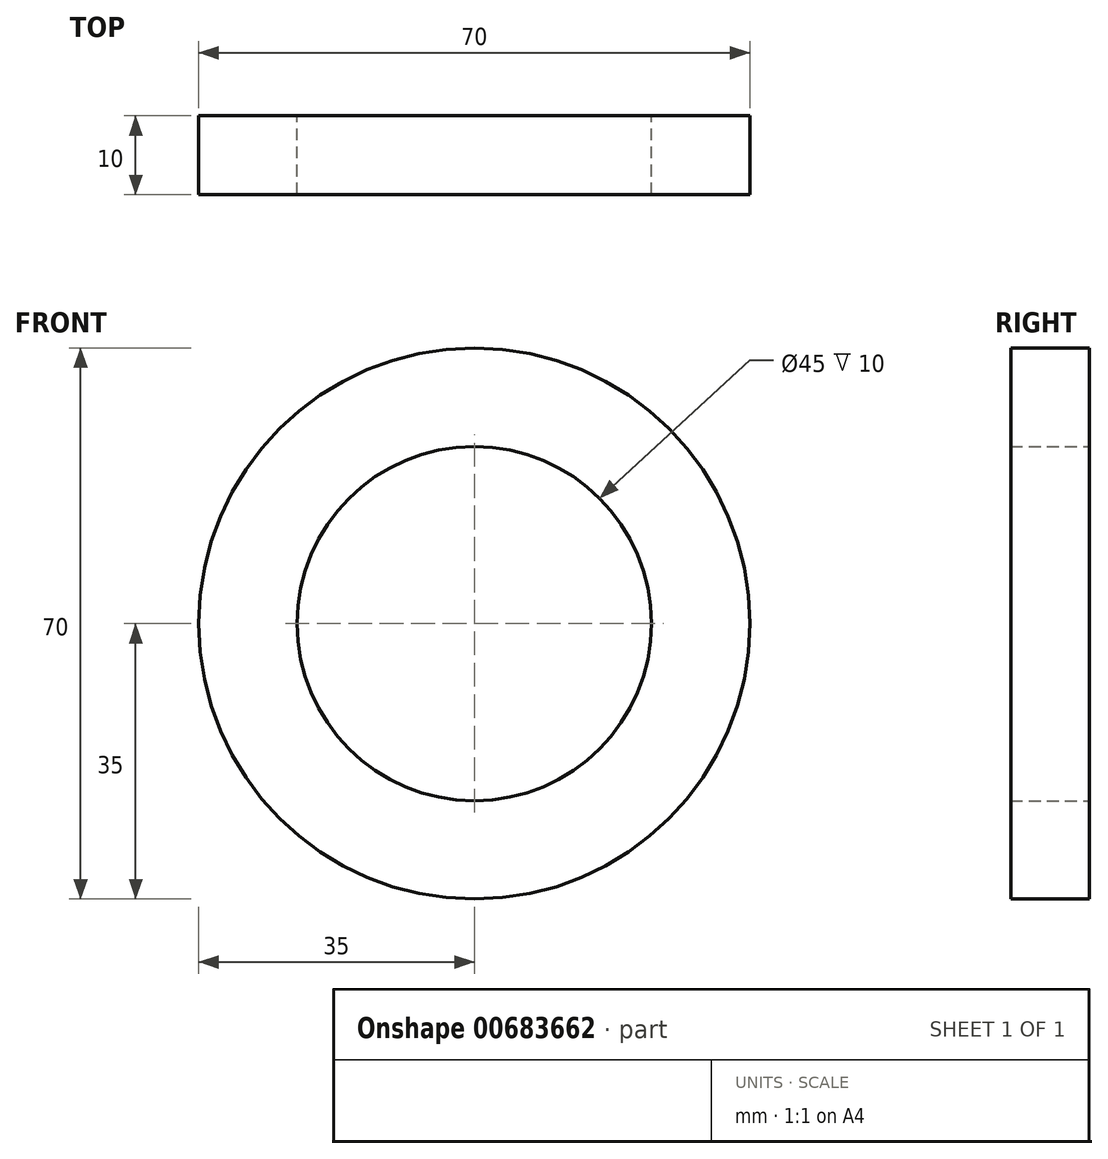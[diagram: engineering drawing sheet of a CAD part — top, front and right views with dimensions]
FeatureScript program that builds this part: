
annotation { "Feature Type Name" : "Feature", "Feature Type Description" : "" }
export const myFeature = defineFeature(function(context is Context, id is Id, definition is map)
    precondition{}
    {
        {
            var Q0;
            Q0=qCreatedBy(makeId("Front.planeOp"),FACE);
            var sketch = newSketch(context, id + "F0", { "sketchPlane" : qUnion([Q0])});
            skCircle(sketch, "E0", {"center": v(0, 0) * mm, "radius": 35 * mm});
            skCircle(sketch, "E1", {"center": v(0, 0) * mm, "radius": 22.5 * mm});
            skSolve(sketch);
        }
        {
            var Q0;
            Q0=makeQuery(id+"F0.imprint","IMPRINT",FACE,{"disambiguationData":[TD([[makeQuery(id+"F0.imprint","IMPRINT",EDGE,{"derivedFrom":sQuery(id+"F0.wireOp",EDGE,"E0")}),1.0]])]});
            extrude(context, id + "F1", {"entities" : qUnion([Q0]), "depth" : 10 * mm, "offsetDistance" : 25 * mm});
        }
    });
